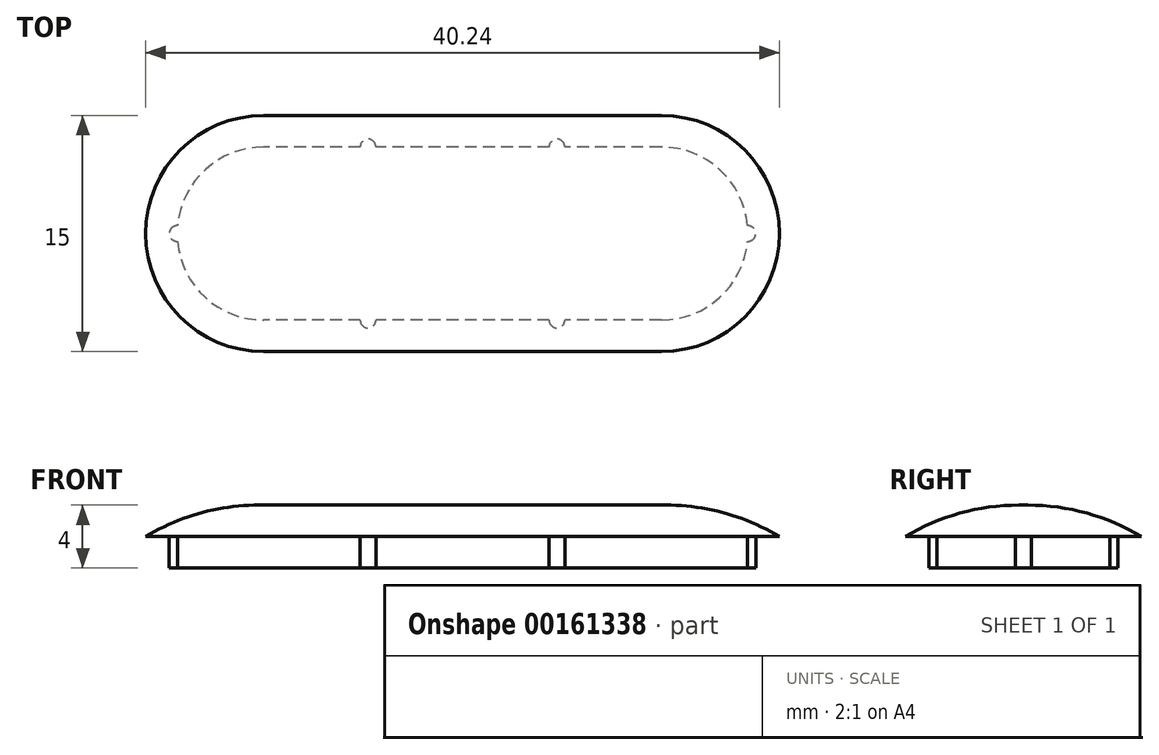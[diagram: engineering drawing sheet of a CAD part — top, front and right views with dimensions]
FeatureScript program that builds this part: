
annotation { "Feature Type Name" : "Feature", "Feature Type Description" : "" }
export const myFeature = defineFeature(function(context is Context, id is Id, definition is map)
    precondition{}
    {
        {
            var Q0;
            Q0=qCreatedBy(makeId("Top.planeOp"),FACE);
            var sketch = newSketch(context, id + "F0", { "sketchPlane" : qUnion([Q0])});
            skLineSegment(sketch, "E0.bottom", {"start": v(12.62, -7.5) * mm, "end": v(-12.62, -7.5) * mm});
            skLineSegment(sketch, "E0.top", {"start": v(12.62, 7.5) * mm, "end": v(-12.62, 7.5) * mm});
            skPoint(sketch, "E0.middle", {"position": v(0, 0) * mm});
            skArc(sketch, "E1", {"start": v(-12.63, 7.5) * mm, "mid": v(-20.13, 0) * mm, "end": v(-12.62, -7.5) * mm});
            skArc(sketch, "E2", {"start": v(12.62, -7.5) * mm, "mid": v(20.13, 0) * mm, "end": v(12.63, 7.5) * mm});
            skSolve(sketch);
        }
        {
            var Q0;
            Q0 = qSketchRegion(id + "F0", true);
            extrude(context, id + "F1", {"entities" : qUnion([Q0]), "depth" : 2 * mm});
        }
        {
            var Q0;
            Q0=makeQuery(id+"F1.opExtrude","CAP_EDGE",EDGE,{"disambiguationData":[OSD([sQuery(id+"F0.wireOp",EDGE,"E0.top")])],"isStart":false});
            fillet(context, id + "F2", {"entities" : qUnion([Q0]), "radius" : 14 * mm, "tangentPropagation" : true, "allowEdgeOverflow" : false});
        }
        {
            var Q0;
            Q0=makeQuery(id+"F1.opExtrude","CAP_FACE",FACE,{"disambiguationData":[OSD([sQuery(id+"F0.wireOp",EDGE,"E0.bottom"),sQuery(id+"F0.wireOp",EDGE,"E0.top"),sQuery(id+"F0.wireOp",EDGE,"E1"),sQuery(id+"F0.wireOp",EDGE,"E2")])],"isStart":true});
            var sketch = newSketch(context, id + "F3", { "sketchPlane" : qUnion([Q0])});
            skLineSegment(sketch, "E3.0", {"start": v(12.62, 5.5) * mm, "end": v(6.5, 5.5) * mm});
            skArc(sketch, "E3.1", {"start": v(12.62, 5.5) * mm, "mid": v(16.33, 4.06) * mm, "end": v(18.1, 0.5) * mm});
            skLineSegment(sketch, "E3.2", {"start": v(12.62, -5.5) * mm, "end": v(6.5, -5.5) * mm});
            skArc(sketch, "E3.3", {"start": v(-12.62, -5.5) * mm, "mid": v(-16.33, -4.06) * mm, "end": v(-18.1, -0.5) * mm});
            skLineSegment(sketch, "E4.bottom", {"start": v(6, -6.5) * mm, "end": v(-6, -6.5) * mm, "construction": true});
            skLineSegment(sketch, "E4.top", {"start": v(6, 6.5) * mm, "end": v(-6, 6.5) * mm, "construction": true});
            skLineSegment(sketch, "E4.left", {"start": v(6, -6.5) * mm, "end": v(6, 6.5) * mm, "construction": true});
            skLineSegment(sketch, "E4.right", {"start": v(-6, -6.5) * mm, "end": v(-6, 6.5) * mm, "construction": true});
            skPoint(sketch, "E4.middle", {"position": v(0, 0) * mm});
            skArc(sketch, "E5", {"start": v(-5.5, 5.5) * mm, "mid": v(-6, 6) * mm, "end": v(-6.5, 5.5) * mm});
            skArc(sketch, "E6", {"start": v(6.5, 5.5) * mm, "mid": v(6, 6) * mm, "end": v(5.5, 5.5) * mm});
            skArc(sketch, "E7", {"start": v(18.1, -0.5) * mm, "mid": v(18.63, 0) * mm, "end": v(18.1, 0.5) * mm});
            skArc(sketch, "E8", {"start": v(5.5, -5.5) * mm, "mid": v(6, -6) * mm, "end": v(6.5, -5.5) * mm});
            skArc(sketch, "E9", {"start": v(-6.5, -5.5) * mm, "mid": v(-6, -6) * mm, "end": v(-5.5, -5.5) * mm});
            skArc(sketch, "E10", {"start": v(-18.1, 0.5) * mm, "mid": v(-18.63, 0) * mm, "end": v(-18.1, -0.5) * mm});
            skLineSegment(sketch, "E11.trimOffspring", {"start": v(-6.5, 5.5) * mm, "end": v(-12.62, 5.5) * mm});
            skLineSegment(sketch, "E12.trimOffspring", {"start": v(5.5, 5.5) * mm, "end": v(-5.5, 5.5) * mm});
            skArc(sketch, "E13.trimOffspring", {"start": v(18.1, -0.5) * mm, "mid": v(16.33, -4.06) * mm, "end": v(12.62, -5.5) * mm});
            skLineSegment(sketch, "E14.trimOffspring", {"start": v(5.5, -5.5) * mm, "end": v(-5.5, -5.5) * mm});
            skLineSegment(sketch, "E15.trimOffspring", {"start": v(-6.5, -5.5) * mm, "end": v(-12.62, -5.5) * mm});
            skArc(sketch, "E16.trimOffspring", {"start": v(-18.1, 0.5) * mm, "mid": v(-16.33, 4.06) * mm, "end": v(-12.62, 5.5) * mm});
            skSolve(sketch);
        }
        {
            var Q0;
            Q0 = qSketchRegion(id + "F3", true);
            extrude(context, id + "F4", {"entities" : qUnion([Q0]), "operationType" : NewBodyOperationType.ADD, "depth" : 2 * mm});
        }
    });
